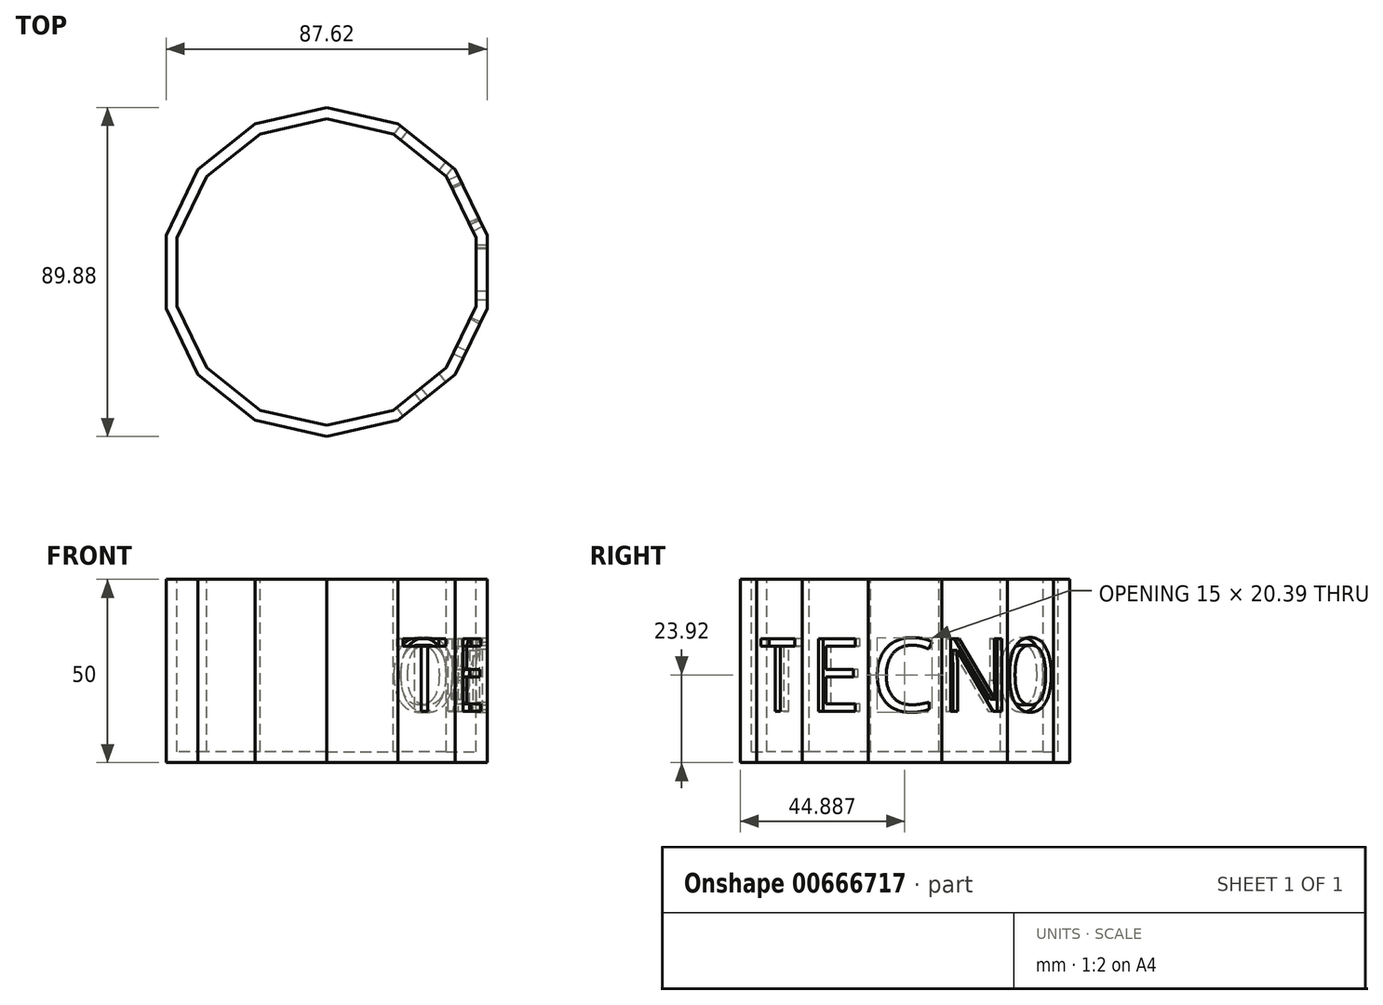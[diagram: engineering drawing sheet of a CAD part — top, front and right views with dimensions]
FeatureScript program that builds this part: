
annotation { "Feature Type Name" : "Feature", "Feature Type Description" : "" }
export const myFeature = defineFeature(function(context is Context, id is Id, definition is map)
    precondition{}
    {
        {
            var Q0;
            Q0=qCreatedBy(makeId("Top.planeOp"),FACE);
            var sketch = newSketch(context, id + "F0", { "sketchPlane" : qUnion([Q0])});
            skCircle(sketch, "E0.cCircle", {"center": v(0, 0) * mm, "radius": 44.94 * mm, "construction": true});
            skLineSegment(sketch, "E0.0", {"start": v(0, -44.94) * mm, "end": v(-19.5, -40.49) * mm});
            skLineSegment(sketch, "E0.1", {"start": v(-19.5, -40.49) * mm, "end": v(-35.14, -28.02) * mm});
            skLineSegment(sketch, "E0.2", {"start": v(-35.14, -28.02) * mm, "end": v(-43.81, -10) * mm});
            skLineSegment(sketch, "E0.3", {"start": v(-43.81, -10) * mm, "end": v(-43.81, 10) * mm});
            skLineSegment(sketch, "E0.4", {"start": v(-43.81, 10) * mm, "end": v(-35.14, 28.02) * mm});
            skLineSegment(sketch, "E0.5", {"start": v(-35.14, 28.02) * mm, "end": v(-19.5, 40.49) * mm});
            skLineSegment(sketch, "E0.6", {"start": v(-19.5, 40.49) * mm, "end": v(0, 44.94) * mm});
            skLineSegment(sketch, "E0.7", {"start": v(0, 44.94) * mm, "end": v(19.5, 40.49) * mm});
            skLineSegment(sketch, "E0.8", {"start": v(19.5, 40.49) * mm, "end": v(35.14, 28.02) * mm});
            skLineSegment(sketch, "E0.9", {"start": v(35.14, 28.02) * mm, "end": v(43.81, 10) * mm});
            skLineSegment(sketch, "E0.10", {"start": v(43.81, 10) * mm, "end": v(43.81, -10) * mm});
            skLineSegment(sketch, "E0.11", {"start": v(43.81, -10) * mm, "end": v(35.14, -28.02) * mm});
            skLineSegment(sketch, "E0.12", {"start": v(35.14, -28.02) * mm, "end": v(19.5, -40.49) * mm});
            skLineSegment(sketch, "E0.13", {"start": v(19.5, -40.49) * mm, "end": v(0, -44.94) * mm});
            skSolve(sketch);
        }
        {
            var Q0;
            Q0=qCreatedBy(makeId("Top.planeOp"),FACE);
            cPlane(context, id + "F1", {"entities" : qUnion([Q0]), "cplaneType" : CPlaneType.OFFSET, "offset" : 50 * mm, "width" : 150 * mm, "height" : 150 * mm});
        }
        {
            var Q0;
            Q0=qCreatedBy(id+"F1.planeOp",FACE);
            var sketch = newSketch(context, id + "F2", { "sketchPlane" : qUnion([Q0])});
            skCircle(sketch, "E1.cCircle", {"center": v(0, 0) * mm, "radius": 44.94 * mm, "construction": true});
            skLineSegment(sketch, "E1.0", {"start": v(0, 44.94) * mm, "end": v(19.5, 40.49) * mm});
            skLineSegment(sketch, "E1.1", {"start": v(19.5, 40.49) * mm, "end": v(35.14, 28.02) * mm});
            skLineSegment(sketch, "E1.2", {"start": v(35.14, 28.02) * mm, "end": v(43.81, 10) * mm});
            skLineSegment(sketch, "E1.3", {"start": v(43.81, 10) * mm, "end": v(43.81, -10) * mm});
            skLineSegment(sketch, "E1.4", {"start": v(43.81, -10) * mm, "end": v(35.14, -28.02) * mm});
            skLineSegment(sketch, "E1.5", {"start": v(35.14, -28.02) * mm, "end": v(19.5, -40.49) * mm});
            skLineSegment(sketch, "E1.6", {"start": v(19.5, -40.49) * mm, "end": v(0, -44.94) * mm});
            skLineSegment(sketch, "E1.7", {"start": v(0, -44.94) * mm, "end": v(-19.5, -40.49) * mm});
            skLineSegment(sketch, "E1.8", {"start": v(-19.5, -40.49) * mm, "end": v(-35.14, -28.02) * mm});
            skLineSegment(sketch, "E1.9", {"start": v(-35.14, -28.02) * mm, "end": v(-43.81, -10) * mm});
            skLineSegment(sketch, "E1.10", {"start": v(-43.81, -10) * mm, "end": v(-43.81, 10) * mm});
            skLineSegment(sketch, "E1.11", {"start": v(-43.81, 10) * mm, "end": v(-35.14, 28.02) * mm});
            skLineSegment(sketch, "E1.12", {"start": v(-35.14, 28.02) * mm, "end": v(-19.5, 40.49) * mm});
            skLineSegment(sketch, "E1.13", {"start": v(-19.5, 40.49) * mm, "end": v(0, 44.94) * mm});
            skSolve(sketch);
        }
        {
            var Q0;
            Q0=makeQuery(id+"F0.imprint","IMPRINT",FACE,{"disambiguationData":[TD([[makeQuery(id+"F0.imprint","IMPRINT",EDGE,{"derivedFrom":sQuery(id+"F0.wireOp",EDGE,"E0.0")}),-1.0]])]});
            var Q1;
            Q1=makeQuery(id+"F2.imprint","IMPRINT",FACE,{"disambiguationData":[TD([[makeQuery(id+"F2.imprint","IMPRINT",EDGE,{"derivedFrom":sQuery(id+"F2.wireOp",EDGE,"E1.0")}),-1.0]])]});
            loft(context, id + "F3", {"sheetProfilesArray" : [{ "sheetProfileEntities" : qUnion([Q0]) }, { "sheetProfileEntities" : qUnion([Q1]) }]});
        }
        {
            var Q0;
            Q0=makeQuery(id+"F3.opLoft","CAP_FACE",FACE,{"disambiguationData":[OSD([makeQuery(id+"F2.imprint","IMPRINT",FACE,{"disambiguationData":[TD([[makeQuery(id+"F2.imprint","IMPRINT",EDGE,{"derivedFrom":sQuery(id+"F2.wireOp",EDGE,"E1.0")}),-1.0]])]})])],"isStart":true});
            shell(context, id + "F4", {"entities" : qUnion([Q0]), "thickness" : 3 * mm});
        }
        {
            var Q0;
            Q0=makeQuery(id+"F3.opLoft","SWEPT_FACE",FACE,{"disambiguationData":[OSD([sQuery(id+"F0.wireOp",EDGE,"E0.10"),sQuery(id+"F0.wireOp",EDGE,"E0.11"),sQuery(id+"F0.wireOp",EDGE,"E0.12"),sQuery(id+"F2.wireOp",EDGE,"E1.3"),sQuery(id+"F2.wireOp",EDGE,"E1.4"),sQuery(id+"F2.wireOp",EDGE,"E1.5")])]});
            var sketch = newSketch(context, id + "F5", { "sketchPlane" : qUnion([Q0])});
            skText(sketch, "E2", { "text": "E", "fontName": "OpenSans-Regular.ttf"});
            const initialGuessF5  = {"E2": [-0.0078, 0.014, 1, 0, 0.02]};
            skSetInitialGuess(sketch, initialGuessF5);
            skSolve(sketch);
        }
        {
            var Q0;
            Q0=qSketchRegion(id+"F5",true);
            extrude(context, id + "F6", {"entities" : qUnion([Q0]), "operationType" : NewBodyOperationType.REMOVE, "oppositeDirection" : true, "depth" : 25 * mm, "offsetDistance" : 25 * mm});
        }
        {
            var Q0;
            Q0=makeQuery(id+"F3.opLoft","SWEPT_FACE",FACE,{"disambiguationData":[OSD([sQuery(id+"F0.wireOp",EDGE,"E0.9"),sQuery(id+"F0.wireOp",EDGE,"E0.10"),sQuery(id+"F0.wireOp",EDGE,"E0.11"),sQuery(id+"F2.wireOp",EDGE,"E1.2"),sQuery(id+"F2.wireOp",EDGE,"E1.3"),sQuery(id+"F2.wireOp",EDGE,"E1.4")])]});
            var sketch = newSketch(context, id + "F7", { "sketchPlane" : qUnion([Q0])});
            skText(sketch, "E3", { "text": "C\n", "fontName": "OpenSans-Regular.ttf"});
            const initialGuessF7  = {"E3": [-0.00925, 0.014, 1, 0, 0.02]};
            skSetInitialGuess(sketch, initialGuessF7);
            skSolve(sketch);
        }
        {
            var Q0;
            Q0=qSketchRegion(id+"F7",true);
            extrude(context, id + "F8", {"entities" : qUnion([Q0]), "operationType" : NewBodyOperationType.REMOVE, "oppositeDirection" : true, "depth" : 25 * mm, "offsetDistance" : 25 * mm});
        }
        {
            var Q0;
            Q0=makeQuery(id+"F3.opLoft","SWEPT_FACE",FACE,{"disambiguationData":[OSD([sQuery(id+"F0.wireOp",EDGE,"E0.8"),sQuery(id+"F0.wireOp",EDGE,"E0.9"),sQuery(id+"F0.wireOp",EDGE,"E0.10"),sQuery(id+"F2.wireOp",EDGE,"E1.1"),sQuery(id+"F2.wireOp",EDGE,"E1.2"),sQuery(id+"F2.wireOp",EDGE,"E1.3")])]});
            var sketch = newSketch(context, id + "F9", { "sketchPlane" : qUnion([Q0])});
            skText(sketch, "E4", { "text": "N", "fontName": "OpenSans-Regular.ttf"});
            const initialGuessF9  = {"E4": [-0.01, 0.014, 1, 0, 0.02]};
            skSetInitialGuess(sketch, initialGuessF9);
            skSolve(sketch);
        }
        {
            var Q0;
            Q0=qSketchRegion(id+"F9",true);
            extrude(context, id + "F10", {"entities" : qUnion([Q0]), "operationType" : NewBodyOperationType.REMOVE, "oppositeDirection" : true, "depth" : 25 * mm, "offsetDistance" : 25 * mm});
        }
        {
            var Q0;
            Q0=makeQuery(id+"F3.opLoft","SWEPT_FACE",FACE,{"disambiguationData":[OSD([sQuery(id+"F0.wireOp",EDGE,"E0.7"),sQuery(id+"F0.wireOp",EDGE,"E0.8"),sQuery(id+"F0.wireOp",EDGE,"E0.9"),sQuery(id+"F2.wireOp",EDGE,"E1.0"),sQuery(id+"F2.wireOp",EDGE,"E1.1"),sQuery(id+"F2.wireOp",EDGE,"E1.2")])]});
            var sketch = newSketch(context, id + "F11", { "sketchPlane" : qUnion([Q0])});
            skText(sketch, "E5", { "text": "O\n", "fontName": "OpenSans-Regular.ttf"});
            const initialGuessF11  = {"E5": [-0.01087, 0.014, 1, 0, 0.02]};
            skSetInitialGuess(sketch, initialGuessF11);
            skSolve(sketch);
        }
        {
            var Q0;
            Q0=qSketchRegion(id+"F11",true);
            extrude(context, id + "F12", {"entities" : qUnion([Q0]), "operationType" : NewBodyOperationType.REMOVE, "oppositeDirection" : true, "depth" : 25 * mm, "offsetDistance" : 25 * mm});
        }
        {
            var Q0;
            Q0=makeQuery(id+"F3.opLoft","SWEPT_FACE",FACE,{"disambiguationData":[OSD([sQuery(id+"F0.wireOp",EDGE,"E0.11"),sQuery(id+"F0.wireOp",EDGE,"E0.12"),sQuery(id+"F0.wireOp",EDGE,"E0.13"),sQuery(id+"F2.wireOp",EDGE,"E1.4"),sQuery(id+"F2.wireOp",EDGE,"E1.5"),sQuery(id+"F2.wireOp",EDGE,"E1.6")])]});
            var sketch = newSketch(context, id + "F13", { "sketchPlane" : qUnion([Q0])});
            skText(sketch, "E6", { "text": "T", "fontName": "OpenSans-Regular.ttf"});
            const initialGuessF13  = {"E6": [-0.00845, 0.014, 1, 0, 0.02]};
            skSetInitialGuess(sketch, initialGuessF13);
            skSolve(sketch);
        }
        {
            var Q0;
            Q0=qSketchRegion(id+"F13",true);
            extrude(context, id + "F14", {"entities" : qUnion([Q0]), "operationType" : NewBodyOperationType.REMOVE, "oppositeDirection" : true, "depth" : 25 * mm, "offsetDistance" : 25 * mm});
        }
    });
